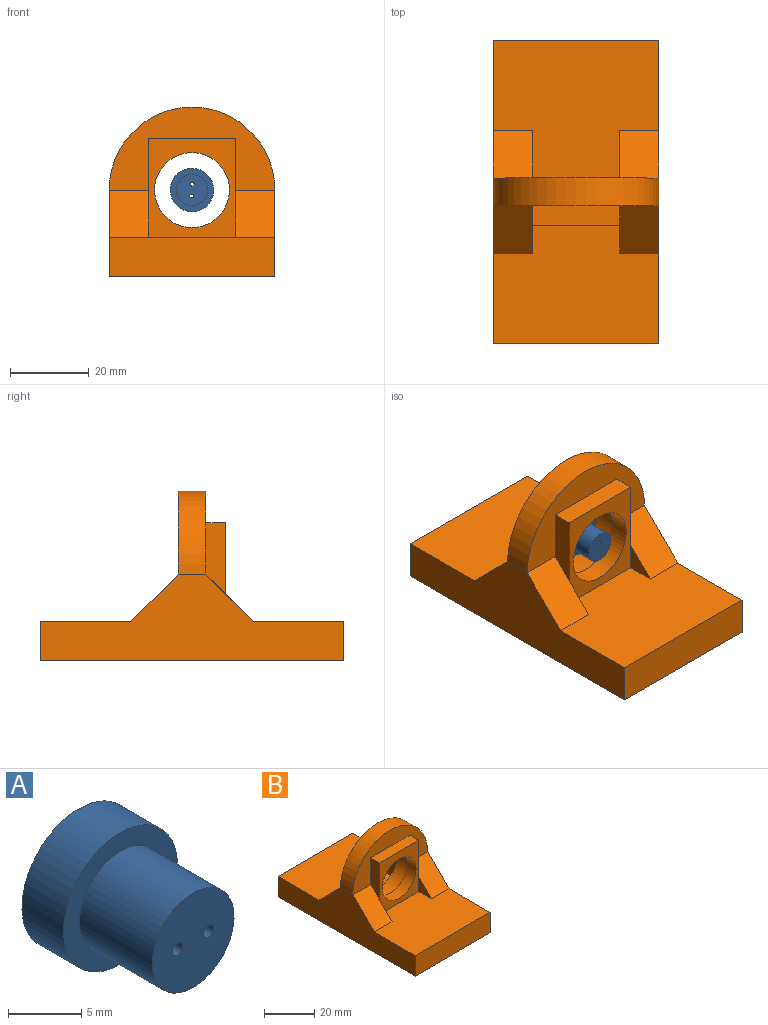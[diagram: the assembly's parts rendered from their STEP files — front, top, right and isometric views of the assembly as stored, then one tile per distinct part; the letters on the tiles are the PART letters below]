
ASSEMBLY  parts=2 mates=1
PART A: 7 faces, bbox 11x11x11 mm
  f0: cylinder r=0.5mm len=11mm, axis (0,-1,0), area 34.6mm2, adj f3,f6
  f1: cylinder r=5.5mm len=11mm, axis (0,-1,0), area 138.2mm2, adj f3,f4
  f2: cylinder r=0.5mm len=11mm, axis (0,-1,0), area 34.6mm2, adj f3,f6
  f3: plane 11x11mm, normal (0,1,0), area 93.5mm2, adj f0,f1,f2
  f4: plane 11x11mm, normal (0,-1,0), area 46mm2, adj f1,f5
  f5: cylinder r=3.95mm len=7.9mm, axis (0,1,0), area 173.7mm2, adj f4,f6
  f6: plane 7.9x7.9mm, normal (0,-1,0), area 47.4mm2, adj f0,f2,f5
PART B: 26 faces, bbox 42x77x43 mm
  f0: plane 7x7mm, normal (1,0,0), area 24.5mm2, adj f9,f17,f25
  f1: plane 42.02x21.01mm, normal (0,-1,0), area 406.1mm2, adj f5,f6,f12,f17,f21,f22,f23
  f2: plane 77x22mm, normal (1,0,0), area 998mm2, adj f3,f5,f8,f9,f10,f11,f12,f14
  f3: plane 77x42.02mm, normal (0,0,-1), area 3235.5mm2, adj f2,f4,f8,f10
  f4: plane 77x22mm, normal (-1,0,0), area 998mm2, adj f3,f5,f8,f9,f10,f11,f17,f19
  f5: cylinder r=21.01mm len=42.02mm, axis (0,1,0), area 462mm2, adj f1,f2,f4,f7
  f6: cylinder r=11.01mm len=22.02mm, axis (0,1,0), area 484.2mm2, adj f1,f7,f16,f18
  f7: plane 42.02x33.01mm, normal (0,1,0), area 577.8mm2, adj f5,f6,f11,f14,f15,f19,f20
  f8: plane 42.02x10mm, normal (0,-1,0), area 420.2mm2, adj f2,f3,f4,f9
  f9: plane 42.02x30mm, normal (0,0,1), area 1121.2mm2, adj f0,f2,f4,f8,f12,f13,f17,f25
  f10: plane 42.02x10mm, normal (0,1,0), area 420.2mm2, adj f2,f3,f4,f11
  f11: plane 42.02x35mm, normal (0,0,1), area 1231.7mm2, adj f2,f4,f7,f10,f14,f15,f19,f20
  f12: plane 12x12mm, normal (0,-0.71,0.71), area 168mm2, adj f1,f2,f9,f13,f21
  f13: plane 7x7mm, normal (-1,0,0), area 24.5mm2, adj f9,f12,f25
  f14: plane 12x12mm, normal (0,0.71,0.71), area 168mm2, adj f2,f7,f11,f15
  f15: plane 12x12mm, normal (-1,0,0), area 72mm2, adj f7,f11,f14
  f16: plane 22.02x22.02mm, normal (0,1,0), area 97.3mm2, adj f6,f17,f22,f24
  f17: plane 12x12mm, normal (0,-0.71,0.71), area 170mm2, adj f0,f1,f4,f9,f16,f22
  f18: plane 0.66x0.02mm, normal (0,-1,0), area 0mm2, adj f6,f19,f20
  f19: plane 12x12mm, normal (0,0.71,0.71), area 170mm2, adj f4,f7,f11,f18,f20
  f20: plane 12x12mm, normal (1,0,0), area 72mm2, adj f7,f11,f18,f19
  f21: plane 18x5mm, normal (1,0,0), area 77.5mm2, adj f1,f12,f23,f25
  f22: plane 18x5mm, normal (-1,0,0), area 77.5mm2, adj f1,f16,f17,f23,f25
  f23: plane 22.1x5mm, normal (0,0,1), area 110.5mm2, adj f1,f21,f22,f25
  f24: cylinder r=9.5mm len=19mm, axis (0,1,0), area 298.5mm2, adj f16,f25
  f25: plane 25x22.1mm, normal (0,-1,0), area 269mm2, adj f0,f9,f13,f21,f22,f23,f24
PLACE A rot(axis=(0,1,0),92.9deg) t=(14.11,-46.64,-4.41)mm
PLACE B t=(14.11,-41.64,-4.41)mm
MATE revolute A.f5 <-> B.f24  axis (0,-1,0) through (14.11,6.01,-4.41)mm
